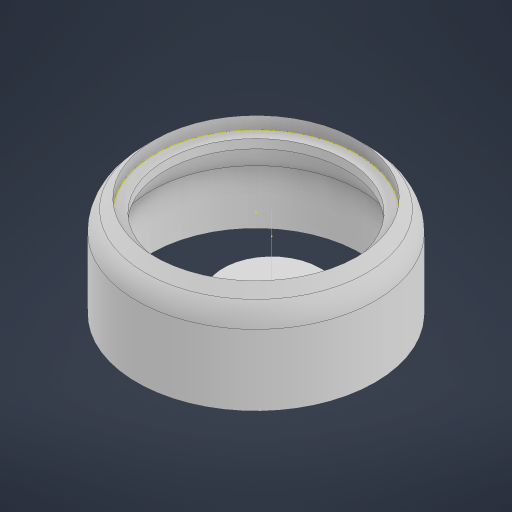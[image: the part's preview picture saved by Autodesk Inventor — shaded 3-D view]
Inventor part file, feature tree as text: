
AUTODESK INVENTOR PART (.ipt)
format: ipt  version: 2023 (Build 270158030, 158C)  size: 297,984 bytes
history: native  units: mm
features: sketch x8, extrude x6, direct_edit x4, move_body x3, shell x2, chamfer x2, fillet x2, other x2, projected_geometry x1
ambient origin geometry x8: Origin, YZ Plane, XZ Plane, XY Plane, X Axis, Y Axis, Z Axis, Center Point
bodies: Solid1 (feature_tree)
feature tree (30):
  extrude  "Extrusion1"  Depth=38.0mm
  extrude  "Extrusion2"  Depth=33.5mm
  shell  "Shell1"  Thickness=4.1mm
  extrude  "Extrusion3"  Depth=10.0mm
  direct_edit  "Direct Edit1"
  chamfer  "Chamfer1"  Distance=8.25mm
  fillet  "Fillet3"  Radius=1.0mm
  other  "Work Axis1"
  sketch  "Sketch9"  dims[d25=2.5mm d26=2.0mm d27=45.0deg d28=4.0mm]
  extrude  "Extrusion8"  Depth=4.0mm
  direct_edit  "Direct Edit4"
  extrude  "Extrusion9"  TaperAngle=0.0deg  [1 undecoded]
  fillet  "Fillet6"  Radius=13.6mm
  shell  "Shell2"  Thickness=2.0mm
  direct_edit  "Direct Edit5"
  extrude  "Extrusion10"  Depth=1.0mm
  chamfer  "Chamfer2"  [1 undecoded]
  direct_edit  "Direct Edit6"
  sketch  "Sketch13"  dims[d49=2.0mm d50=0.0mm d51=2.0mm d52=2.0mm d53=60.0deg d54=0.0mm d55=0.0mm d56=-0.75mm d32=0.5mm d33=0.872665mm d34=0.5mm]
  sketch  "Sketch1"  dims[d0=11.6mm d1=38.0mm]
  sketch  "Sketch2"  dims[d2=38.5mm d3=33.5mm d4=4.1mm d5=0.0mm]
  sketch  "Sketch3"  dims[d6=10.0mm d7=0.0mm d8=1.0mm d9=8.25mm d10=0.0mm d16=1.0mm]
  sketch  "Sketch10"  dims[d35=2.0mm d36=0.0mm d37=0.0mm d38=0.0mm d39=-7.0mm d40=13.6mm d41=2.0mm d42=0.0mm]
  projected_geometry  "Projected Loop2"
  sketch  "Sketch11"  dims[d43=2.0mm d44=1.0mm d45=-1.15mm d46=0.0mm d47=0.0mm]
  sketch  "Sketch12"  dims[d48=2.0mm]
  other  "Size1"
  move_body  "Move3"
  move_body  "Move4"
  move_body  "Move5"
note: 2 required parameter values undecoded (feature->parameter linkage not recoverable at this tier; creation-order binding heuristic only, values carry confidence <= 0.55)
